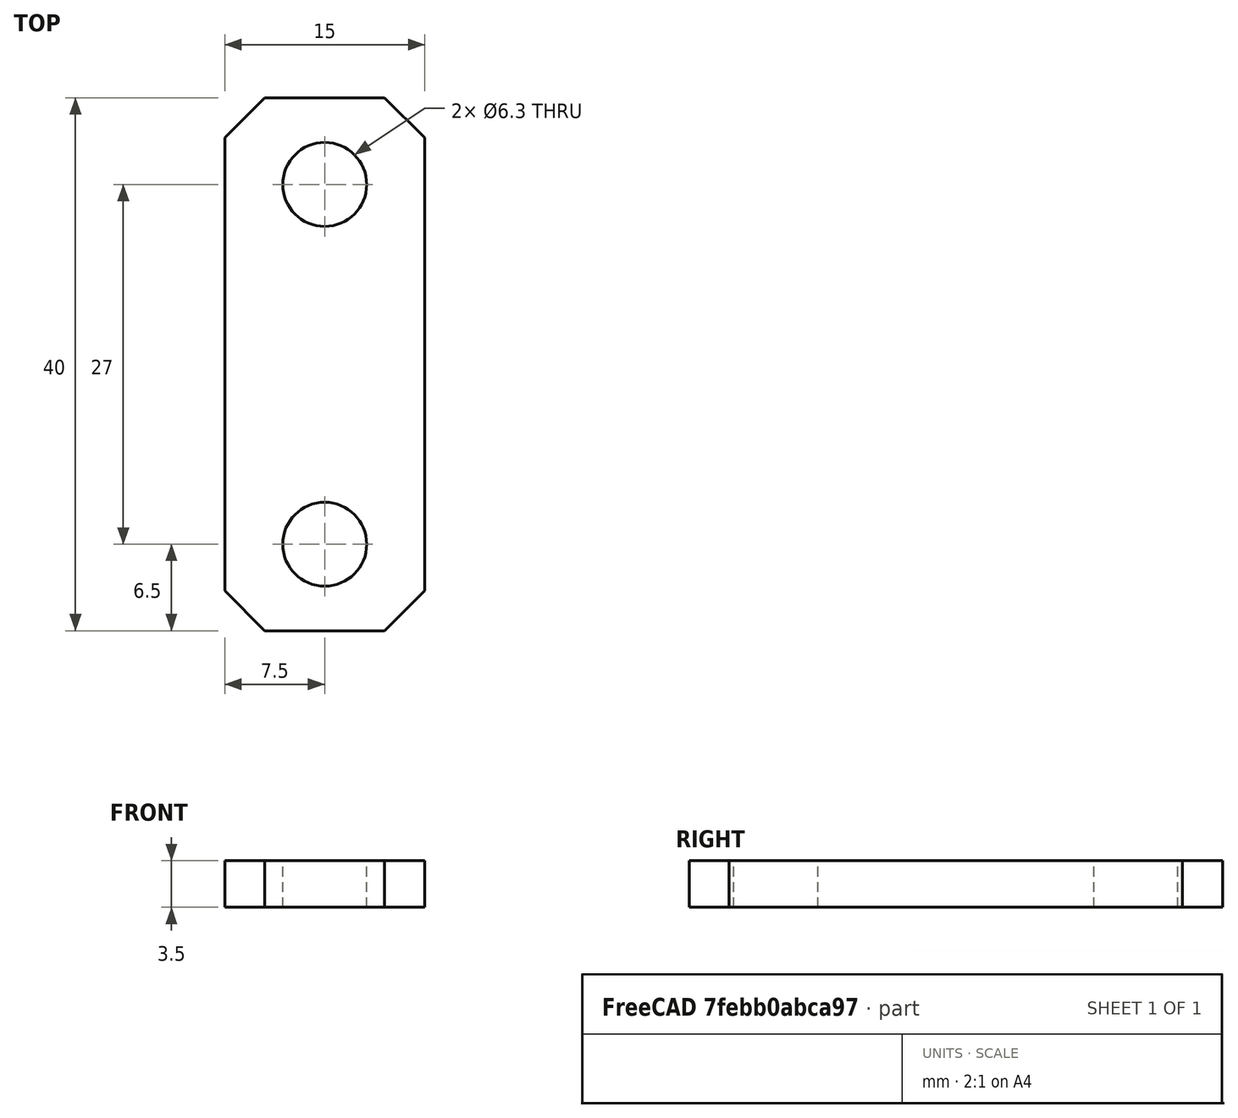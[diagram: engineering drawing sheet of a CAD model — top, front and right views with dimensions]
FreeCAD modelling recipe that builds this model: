
FCSTD DOCUMENT  (FreeCAD 0.15R4671 (Git))
Label: two_tendon_strap_top
License: All rights reserved
LicenseURL: http://en.wikipedia.org/wiki/All_rights_reserved
objects: Part::Cylinder×2, Part::Box×1, Part::MultiFuse×1, Part::Cut×1, Part::Chamfer×1
note: 6 computed .brp shape members not serialized (recipe doc carries the construction recipe); baked Part::Feature solids carry a one-line shape summary decoded from their .brp

FEATURE [Part::Box] Box  label="Cube"
  Height = 3.5
  Length = 15
  Placement = pos=(7.5,0,0) rot=(0,0,1;0rad)
  Width = 40
FEATURE [Part::Cylinder] Cylinder004
  Angle = 360
  Height = 10
  Placement = pos=(15,6.5,-2) rot=(0,0,1;0rad)
  Radius = 3.15
FEATURE [Part::Cylinder] Cylinder005
  Angle = 360
  Height = 10
  Placement = pos=(15,33.5,-2) rot=(0,0,1;0rad)
  Radius = 3.15
FEATURE [Part::MultiFuse] Fusion
  Shapes = -> [Cylinder005,Cylinder004]
FEATURE [Part::Cut] Cut
  Base = -> Box
  Tool = -> Fusion
FEATURE [Part::Chamfer] Chamfer
  Base = -> Cut
  Edges = 4 edges r=3: [Edge1,Edge3,Edge6,Edge13]
